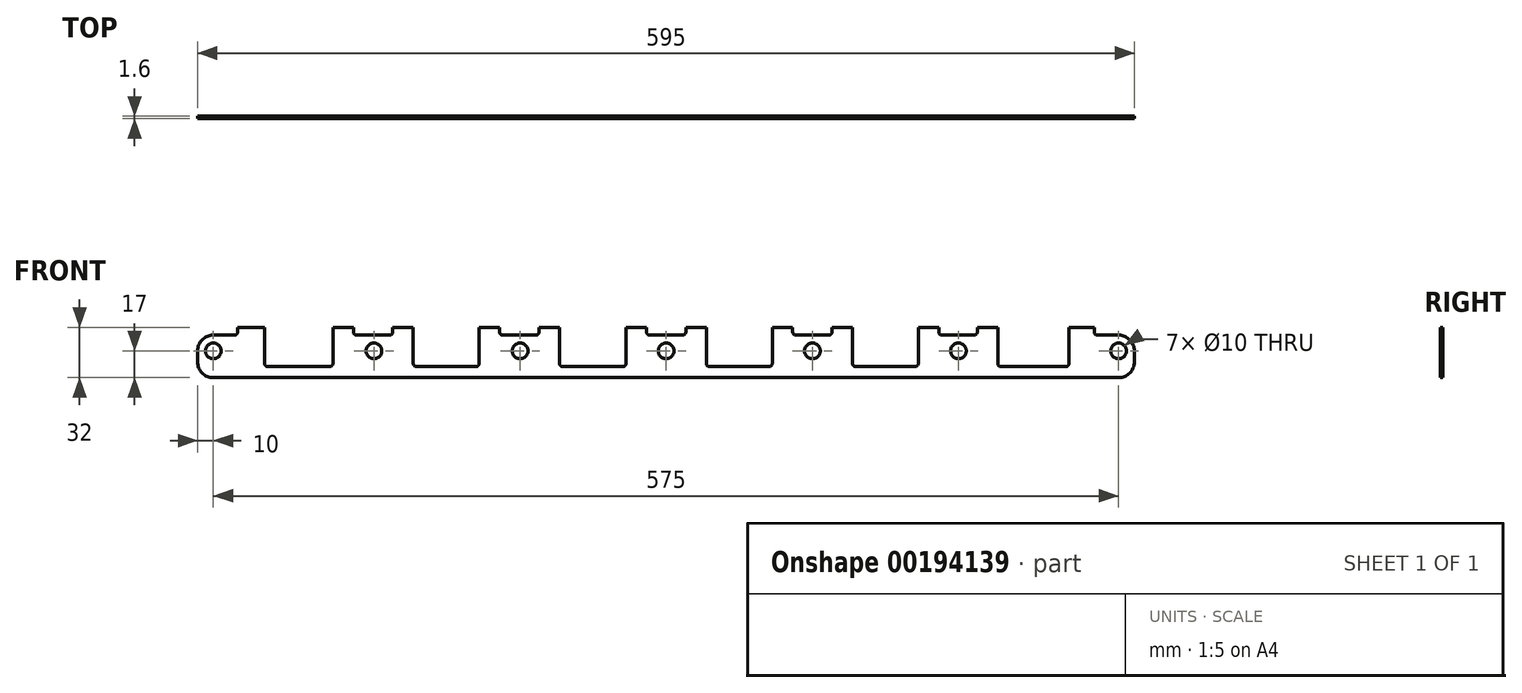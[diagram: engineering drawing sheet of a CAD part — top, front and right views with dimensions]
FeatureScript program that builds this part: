
annotation { "Feature Type Name" : "Feature", "Feature Type Description" : "" }
export const myFeature = defineFeature(function(context is Context, id is Id, definition is map)
    precondition{}
    {
        {
            var Q0;
            Q0=qCreatedBy(makeId("Front.planeOp"),FACE);
            var sketch = newSketch(context, id + "F0", { "sketchPlane" : qUnion([Q0])});
            skCircle(sketch, "E0", {"center": v(0, 0) * mm, "radius": 5 * mm});
            skCircle(sketch, "E1", {"center": v(194.85, 0) * mm, "radius": 5 * mm});
            skCircle(sketch, "E2", {"center": v(380.5, 0) * mm, "radius": 5 * mm});
            skCircle(sketch, "E3", {"center": v(473.25, 0) * mm, "radius": 5 * mm});
            skCircle(sketch, "E4", {"center": v(575, 0) * mm, "radius": 5 * mm});
            skCircle(sketch, "E5", {"center": v(102, 0) * mm, "radius": 5 * mm});
            skCircle(sketch, "E6", {"center": v(287.6, 0) * mm, "radius": 5 * mm});
            skLineSegment(sketch, "E7", {"start": v(0, -17) * mm, "end": v(575, -17) * mm});
            skLineSegment(sketch, "E8", {"start": v(585, -7) * mm, "end": v(585, 0) * mm});
            skLineSegment(sketch, "E9", {"start": v(575, 10) * mm, "end": v(561.5, 10) * mm});
            skLineSegment(sketch, "E10", {"start": v(559.5, 12) * mm, "end": v(559.5, 15) * mm});
            skLineSegment(sketch, "E11", {"start": v(559.5, 15) * mm, "end": v(543.5, 15) * mm});
            skLineSegment(sketch, "E12", {"start": v(543.5, 15) * mm, "end": v(543.5, -8) * mm});
            skLineSegment(sketch, "E13", {"start": v(541.5, -10) * mm, "end": v(500.25, -10) * mm});
            skLineSegment(sketch, "E14", {"start": v(498.25, -8) * mm, "end": v(498.25, 15) * mm});
            skLineSegment(sketch, "E15", {"start": v(498.25, 15) * mm, "end": v(485.25, 15) * mm});
            skLineSegment(sketch, "E16", {"start": v(485.25, 15) * mm, "end": v(485.25, 12) * mm});
            skLineSegment(sketch, "E17", {"start": v(483.25, 10) * mm, "end": v(462.75, 10) * mm});
            skLineSegment(sketch, "E18", {"start": v(460.75, 12) * mm, "end": v(460.75, 15) * mm});
            skLineSegment(sketch, "E19", {"start": v(460.75, 15) * mm, "end": v(447.75, 15) * mm});
            skLineSegment(sketch, "E20", {"start": v(447.75, 15) * mm, "end": v(447.75, -8) * mm});
            skLineSegment(sketch, "E21", {"start": v(445.75, -10) * mm, "end": v(408, -10) * mm});
            skLineSegment(sketch, "E22", {"start": v(406, -8) * mm, "end": v(406, 15) * mm});
            skLineSegment(sketch, "E23", {"start": v(406, 15) * mm, "end": v(393, 15) * mm});
            skLineSegment(sketch, "E24", {"start": v(393, 15) * mm, "end": v(393, 12) * mm});
            skLineSegment(sketch, "E25", {"start": v(391, 10) * mm, "end": v(370, 10) * mm});
            skLineSegment(sketch, "E26", {"start": v(368, 12) * mm, "end": v(368, 15) * mm});
            skLineSegment(sketch, "E27", {"start": v(368, 15) * mm, "end": v(355, 15) * mm});
            skLineSegment(sketch, "E28", {"start": v(355, 15) * mm, "end": v(355, -8) * mm});
            skLineSegment(sketch, "E29", {"start": v(353, -10) * mm, "end": v(315.1, -10) * mm});
            skLineSegment(sketch, "E30", {"start": v(313.1, -8) * mm, "end": v(313.1, 15) * mm});
            skLineSegment(sketch, "E31", {"start": v(313.1, 15) * mm, "end": v(300.1, 15) * mm});
            skLineSegment(sketch, "E32", {"start": v(300.1, 15) * mm, "end": v(300.1, 12) * mm});
            skLineSegment(sketch, "E33", {"start": v(298.1, 10) * mm, "end": v(277.1, 10) * mm});
            skLineSegment(sketch, "E34", {"start": v(275.1, 12) * mm, "end": v(275.1, 15) * mm});
            skLineSegment(sketch, "E35", {"start": v(275.1, 15) * mm, "end": v(262.1, 15) * mm});
            skLineSegment(sketch, "E36", {"start": v(262.1, 15) * mm, "end": v(262.1, -8) * mm});
            skLineSegment(sketch, "E37", {"start": v(260.1, -10) * mm, "end": v(221.85, -10) * mm});
            skLineSegment(sketch, "E38", {"start": v(219.85, -8) * mm, "end": v(219.85, 15) * mm});
            skLineSegment(sketch, "E39", {"start": v(219.85, 15) * mm, "end": v(206.85, 15) * mm});
            skLineSegment(sketch, "E40", {"start": v(206.85, 15) * mm, "end": v(206.85, 12) * mm});
            skLineSegment(sketch, "E41", {"start": v(204.85, 10) * mm, "end": v(183.85, 10) * mm});
            skLineSegment(sketch, "E42", {"start": v(181.85, 12) * mm, "end": v(181.85, 15) * mm});
            skLineSegment(sketch, "E43", {"start": v(181.85, 15) * mm, "end": v(168.85, 15) * mm});
            skLineSegment(sketch, "E44", {"start": v(168.85, 15) * mm, "end": v(168.85, -8) * mm});
            skLineSegment(sketch, "E45", {"start": v(166.85, -10) * mm, "end": v(129, -10) * mm});
            skLineSegment(sketch, "E46", {"start": v(127, -8) * mm, "end": v(127, 15) * mm});
            skLineSegment(sketch, "E47", {"start": v(127, 15) * mm, "end": v(114, 15) * mm});
            skLineSegment(sketch, "E48", {"start": v(114, 15) * mm, "end": v(114, 12) * mm});
            skLineSegment(sketch, "E49", {"start": v(112, 10) * mm, "end": v(91, 10) * mm});
            skLineSegment(sketch, "E50", {"start": v(89, 12) * mm, "end": v(89, 15) * mm});
            skLineSegment(sketch, "E51", {"start": v(89, 15) * mm, "end": v(76, 15) * mm});
            skLineSegment(sketch, "E52", {"start": v(76, 15) * mm, "end": v(76, -8) * mm});
            skLineSegment(sketch, "E53", {"start": v(74, -10) * mm, "end": v(34.5, -10) * mm});
            skLineSegment(sketch, "E54", {"start": v(32.5, -8) * mm, "end": v(32.5, 15) * mm});
            skLineSegment(sketch, "E55", {"start": v(32.5, 15) * mm, "end": v(15.5, 15) * mm});
            skLineSegment(sketch, "E56", {"start": v(15.5, 15) * mm, "end": v(15.5, 12) * mm});
            skLineSegment(sketch, "E57", {"start": v(13.5, 10) * mm, "end": v(0, 10) * mm});
            skLineSegment(sketch, "E58", {"start": v(-10, -7) * mm, "end": v(-10, 0) * mm});
            skPoint(sketch, "E59.visualSharp", {"position": v(-10, 10) * mm});
            skArc(sketch, "E59.filletArc", {"start": v(0, 10) * mm, "mid": v(-7.07, 7.07) * mm, "end": v(-10, 0) * mm});
            skPoint(sketch, "E60.visualSharp", {"position": v(-10, -17) * mm});
            skArc(sketch, "E60.filletArc", {"start": v(-10, -7) * mm, "mid": v(-7.07, -14.07) * mm, "end": v(0, -17) * mm});
            skPoint(sketch, "E61.visualSharp", {"position": v(585, 10) * mm});
            skArc(sketch, "E61.filletArc", {"start": v(585, 0) * mm, "mid": v(582.07, 7.07) * mm, "end": v(575, 10) * mm});
            skPoint(sketch, "E62.visualSharp", {"position": v(585, -17) * mm});
            skArc(sketch, "E62.filletArc", {"start": v(575, -17) * mm, "mid": v(582.07, -14.07) * mm, "end": v(585, -7) * mm});
            skPoint(sketch, "E63.visualSharp", {"position": v(543.5, -10) * mm});
            skArc(sketch, "E63.filletArc", {"start": v(541.5, -10) * mm, "mid": v(542.91, -9.41) * mm, "end": v(543.5, -8) * mm});
            skPoint(sketch, "E64.visualSharp", {"position": v(559.5, 10) * mm});
            skArc(sketch, "E64.filletArc", {"start": v(559.5, 12) * mm, "mid": v(560.09, 10.59) * mm, "end": v(561.5, 10) * mm});
            skPoint(sketch, "E65.visualSharp", {"position": v(498.25, -10) * mm});
            skArc(sketch, "E65.filletArc", {"start": v(498.25, -8) * mm, "mid": v(498.84, -9.41) * mm, "end": v(500.25, -10) * mm});
            skPoint(sketch, "E66.visualSharp", {"position": v(485.25, 10) * mm});
            skArc(sketch, "E66.filletArc", {"start": v(483.25, 10) * mm, "mid": v(484.66, 10.59) * mm, "end": v(485.25, 12) * mm});
            skPoint(sketch, "E67.visualSharp", {"position": v(460.75, 10) * mm});
            skArc(sketch, "E67.filletArc", {"start": v(460.75, 12) * mm, "mid": v(461.34, 10.59) * mm, "end": v(462.75, 10) * mm});
            skPoint(sketch, "E68.visualSharp", {"position": v(447.75, -10) * mm});
            skArc(sketch, "E68.filletArc", {"start": v(445.75, -10) * mm, "mid": v(447.16, -9.41) * mm, "end": v(447.75, -8) * mm});
            skPoint(sketch, "E69.visualSharp", {"position": v(406, -10) * mm});
            skArc(sketch, "E69.filletArc", {"start": v(406, -8) * mm, "mid": v(406.59, -9.41) * mm, "end": v(408, -10) * mm});
            skPoint(sketch, "E70.visualSharp", {"position": v(393, 10) * mm});
            skArc(sketch, "E70.filletArc", {"start": v(391, 10) * mm, "mid": v(392.41, 10.59) * mm, "end": v(393, 12) * mm});
            skPoint(sketch, "E71.visualSharp", {"position": v(368, 10) * mm});
            skArc(sketch, "E71.filletArc", {"start": v(368, 12) * mm, "mid": v(368.59, 10.59) * mm, "end": v(370, 10) * mm});
            skPoint(sketch, "E72.visualSharp", {"position": v(355, -10) * mm});
            skArc(sketch, "E72.filletArc", {"start": v(353, -10) * mm, "mid": v(354.41, -9.41) * mm, "end": v(355, -8) * mm});
            skPoint(sketch, "E73.visualSharp", {"position": v(313.1, -10) * mm});
            skArc(sketch, "E73.filletArc", {"start": v(313.1, -8) * mm, "mid": v(313.69, -9.41) * mm, "end": v(315.1, -10) * mm});
            skPoint(sketch, "E74.visualSharp", {"position": v(300.1, 10) * mm});
            skArc(sketch, "E74.filletArc", {"start": v(298.1, 10) * mm, "mid": v(299.51, 10.59) * mm, "end": v(300.1, 12) * mm});
            skPoint(sketch, "E75.visualSharp", {"position": v(275.1, 10) * mm});
            skArc(sketch, "E75.filletArc", {"start": v(275.1, 12) * mm, "mid": v(275.69, 10.59) * mm, "end": v(277.1, 10) * mm});
            skPoint(sketch, "E76.visualSharp", {"position": v(262.1, -10) * mm});
            skArc(sketch, "E76.filletArc", {"start": v(260.1, -10) * mm, "mid": v(261.51, -9.41) * mm, "end": v(262.1, -8) * mm});
            skPoint(sketch, "E77.visualSharp", {"position": v(219.85, -10) * mm});
            skArc(sketch, "E77.filletArc", {"start": v(219.85, -8) * mm, "mid": v(220.44, -9.41) * mm, "end": v(221.85, -10) * mm});
            skPoint(sketch, "E78.visualSharp", {"position": v(206.85, 10) * mm});
            skArc(sketch, "E78.filletArc", {"start": v(204.85, 10) * mm, "mid": v(206.26, 10.59) * mm, "end": v(206.85, 12) * mm});
            skPoint(sketch, "E79.visualSharp", {"position": v(181.85, 10) * mm});
            skArc(sketch, "E79.filletArc", {"start": v(181.85, 12) * mm, "mid": v(182.44, 10.59) * mm, "end": v(183.85, 10) * mm});
            skPoint(sketch, "E80.visualSharp", {"position": v(168.85, -10) * mm});
            skArc(sketch, "E80.filletArc", {"start": v(166.85, -10) * mm, "mid": v(168.26, -9.41) * mm, "end": v(168.85, -8) * mm});
            skPoint(sketch, "E81.visualSharp", {"position": v(127, -10) * mm});
            skArc(sketch, "E81.filletArc", {"start": v(127, -8) * mm, "mid": v(127.59, -9.41) * mm, "end": v(129, -10) * mm});
            skPoint(sketch, "E82.visualSharp", {"position": v(114, 10) * mm});
            skArc(sketch, "E82.filletArc", {"start": v(112, 10) * mm, "mid": v(113.41, 10.59) * mm, "end": v(114, 12) * mm});
            skPoint(sketch, "E83.visualSharp", {"position": v(89, 10) * mm});
            skArc(sketch, "E83.filletArc", {"start": v(89, 12) * mm, "mid": v(89.59, 10.59) * mm, "end": v(91, 10) * mm});
            skPoint(sketch, "E84.visualSharp", {"position": v(76, -10) * mm});
            skArc(sketch, "E84.filletArc", {"start": v(74, -10) * mm, "mid": v(75.41, -9.41) * mm, "end": v(76, -8) * mm});
            skPoint(sketch, "E85.visualSharp", {"position": v(32.5, -10) * mm});
            skArc(sketch, "E85.filletArc", {"start": v(32.5, -8) * mm, "mid": v(33.09, -9.41) * mm, "end": v(34.5, -10) * mm});
            skPoint(sketch, "E86.visualSharp", {"position": v(15.5, 10) * mm});
            skArc(sketch, "E86.filletArc", {"start": v(13.5, 10) * mm, "mid": v(14.91, 10.59) * mm, "end": v(15.5, 12) * mm});
            skSolve(sketch);
        }
        {
            var Q0;
            Q0=makeQuery(id+"F0.imprint","IMPRINT",FACE,{"disambiguationData":[TD([[makeQuery(id+"F0.imprint","IMPRINT",EDGE,{"derivedFrom":sQuery(id+"F0.wireOp",EDGE,"E0")}),-1.0]])]});
            extrude(context, id + "F1", {"entities" : qUnion([Q0]), "depth" : 1.6 * mm});
        }
    });
